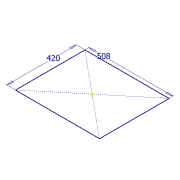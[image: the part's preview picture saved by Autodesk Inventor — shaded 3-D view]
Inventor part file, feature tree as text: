
AUTODESK INVENTOR PART (.ipt)
format: ipt  version: 2016 SP2 (Build 200236200, 236)  size: 91,136 bytes
history: native  units: mm
features: extrude x2, sketch x2
ambient origin geometry x8: Origin, YZ Plane, XZ Plane, XY Plane, X Axis, Y Axis, Z Axis, Center Point
bodies: Body1 (feature_tree)
feature tree (4):
  extrude  "Extrusion3"  Depth=508.0mm
  extrude  "Extrusion4"  Depth=450.0mm
  sketch  "Sketch1"  dims[d4=420.0mm d5=508.0mm]
  sketch  "Sketch2"  dims[d6=459.994mm d7=0.0mm d8=450.0mm d9=352.0mm d10=459.994mm d11=0.0mm]
